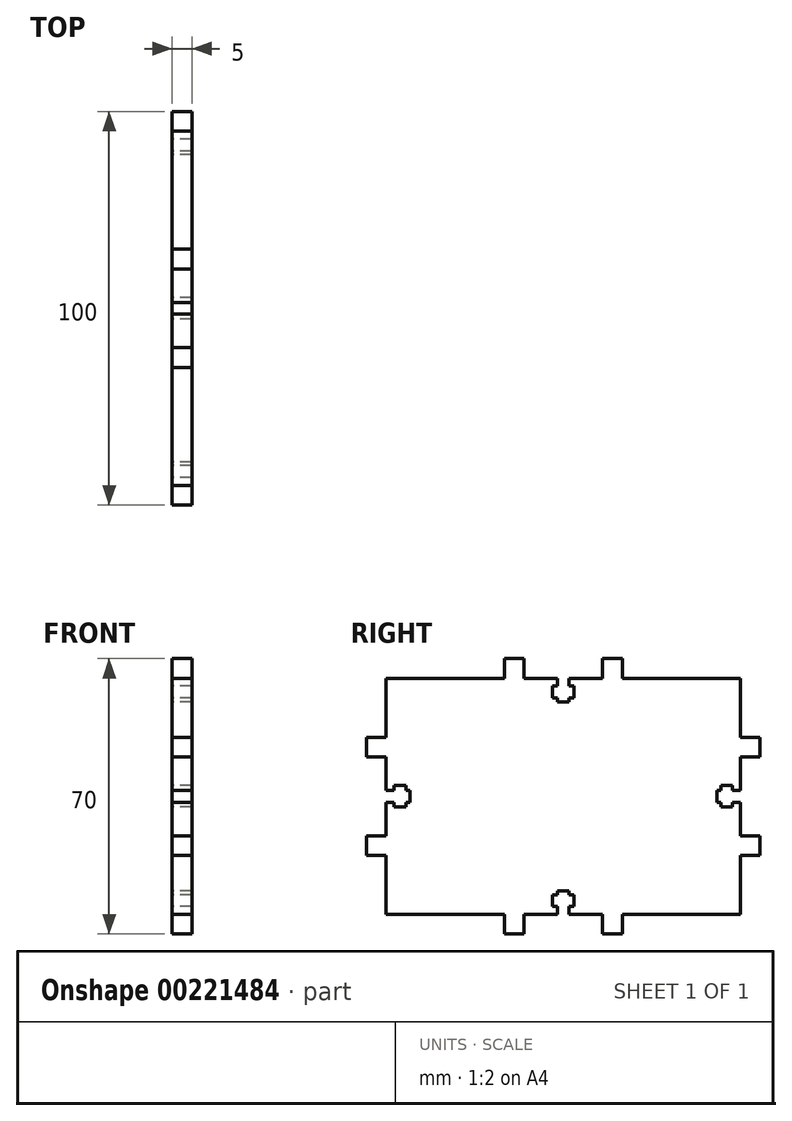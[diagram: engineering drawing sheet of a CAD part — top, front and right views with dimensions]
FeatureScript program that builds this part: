
annotation { "Feature Type Name" : "Feature", "Feature Type Description" : "" }
export const myFeature = defineFeature(function(context is Context, id is Id, definition is map)
    precondition{}
    {
        {
            assignVariable(context, id + "F0", {"name" : "thickness", "anyValue" : 5 * mm});
        }
        {
            var Q0;
            Q0=qCreatedBy(makeId("Right.planeOp"),FACE);
            var sketch = newSketch(context, id + "F1", { "sketchPlane" : qUnion([Q0])});
            skLineSegment(sketch, "E0.bottom", {"start": v(0, 0) * mm, "end": v(30, 0) * mm});
            skLineSegment(sketch, "E0.top", {"start": v(0, 60) * mm, "end": v(30, 60) * mm});
            skLineSegment(sketch, "E0.left", {"start": v(0, 0) * mm, "end": v(0, 15) * mm});
            skLineSegment(sketch, "E0.right", {"start": v(90, 0) * mm, "end": v(90, 15) * mm});
            skLineSegment(sketch, "E1", {"start": v(0, 45) * mm, "end": v(-5, 45) * mm});
            skLineSegment(sketch, "E2", {"start": v(-5, 45) * mm, "end": v(-5, 40) * mm});
            skLineSegment(sketch, "E3", {"start": v(-5, 40) * mm, "end": v(0, 40) * mm});
            skLineSegment(sketch, "E4", {"start": v(0, 20) * mm, "end": v(-5, 20) * mm});
            skLineSegment(sketch, "E5", {"start": v(-5, 20) * mm, "end": v(-5, 15) * mm});
            skLineSegment(sketch, "E6", {"start": v(-5, 15) * mm, "end": v(0, 15) * mm});
            skLineSegment(sketch, "E7", {"start": v(45, 60) * mm, "end": v(45, 0) * mm, "construction": true});
            skLineSegment(sketch, "E8", {"start": v(90, 30) * mm, "end": v(0, 30) * mm, "construction": true});
            skLineSegment(sketch, "E9", {"start": v(0, 31.5) * mm, "end": v(2, 31.5) * mm});
            skLineSegment(sketch, "E10", {"start": v(2, 31.5) * mm, "end": v(2, 32.75) * mm});
            skLineSegment(sketch, "E11", {"start": v(2, 32.75) * mm, "end": v(5, 32.75) * mm});
            skLineSegment(sketch, "E12", {"start": v(5, 32.75) * mm, "end": v(5, 31.5) * mm});
            skLineSegment(sketch, "E13", {"start": v(5, 27.25) * mm, "end": v(2, 27.25) * mm});
            skLineSegment(sketch, "E14", {"start": v(2, 27.25) * mm, "end": v(2, 28.5) * mm});
            skLineSegment(sketch, "E15", {"start": v(2, 28.5) * mm, "end": v(0, 28.5) * mm});
            skLineSegment(sketch, "E16", {"start": v(5, 31.5) * mm, "end": v(6, 31.5) * mm});
            skLineSegment(sketch, "E17", {"start": v(6, 31.5) * mm, "end": v(6, 28.5) * mm});
            skLineSegment(sketch, "E18", {"start": v(6, 28.5) * mm, "end": v(5, 28.5) * mm});
            skLineSegment(sketch, "E19.trimOffspring", {"start": v(5, 28.5) * mm, "end": v(5, 27.25) * mm});
            skPoint(sketch, "E20", {"position": v(6, 30) * mm});
            skLineSegment(sketch, "E21.MirrorCS", {"start": v(85, 31.5) * mm, "end": v(84, 31.5) * mm});
            skLineSegment(sketch, "E22.MirrorCS", {"start": v(88, 31.5) * mm, "end": v(88, 32.75) * mm});
            skLineSegment(sketch, "E23.MirrorCS", {"start": v(84, 28.5) * mm, "end": v(85, 28.5) * mm});
            skLineSegment(sketch, "E24.MirrorCS", {"start": v(88, 27.25) * mm, "end": v(88, 28.5) * mm});
            skLineSegment(sketch, "E25.MirrorCS", {"start": v(85, 32.75) * mm, "end": v(85, 31.5) * mm});
            skLineSegment(sketch, "E26.MirrorCS", {"start": v(85, 28.5) * mm, "end": v(85, 27.25) * mm});
            skLineSegment(sketch, "E27.MirrorCS", {"start": v(88, 28.5) * mm, "end": v(90, 28.5) * mm});
            skLineSegment(sketch, "E28.MirrorCS", {"start": v(84, 31.5) * mm, "end": v(84, 28.5) * mm});
            skLineSegment(sketch, "E29.MirrorCS", {"start": v(90, 31.5) * mm, "end": v(88, 31.5) * mm});
            skPoint(sketch, "E30.MirrorP", {"position": v(84, 30) * mm});
            skLineSegment(sketch, "E31.MirrorCS", {"start": v(85, 27.25) * mm, "end": v(88, 27.25) * mm});
            skLineSegment(sketch, "E32.MirrorCS", {"start": v(90, 45) * mm, "end": v(95, 45) * mm});
            skLineSegment(sketch, "E33.MirrorCS", {"start": v(95, 45) * mm, "end": v(95, 40) * mm});
            skLineSegment(sketch, "E34.MirrorCS", {"start": v(95, 40) * mm, "end": v(90, 40) * mm});
            skLineSegment(sketch, "E35.MirrorCS", {"start": v(88, 32.75) * mm, "end": v(85, 32.75) * mm});
            skLineSegment(sketch, "E36.MirrorCS", {"start": v(95, 15) * mm, "end": v(90, 15) * mm});
            skLineSegment(sketch, "E37.MirrorCS", {"start": v(90, 20) * mm, "end": v(95, 20) * mm});
            skLineSegment(sketch, "E38.MirrorCS", {"start": v(95, 20) * mm, "end": v(95, 15) * mm});
            skLineSegment(sketch, "E39", {"start": v(30, 0) * mm, "end": v(30, -5) * mm});
            skLineSegment(sketch, "E40", {"start": v(30, -5) * mm, "end": v(35, -5) * mm});
            skLineSegment(sketch, "E41", {"start": v(35, -5) * mm, "end": v(35, 0) * mm});
            skLineSegment(sketch, "E42", {"start": v(55, 0) * mm, "end": v(55, -5) * mm});
            skLineSegment(sketch, "E43", {"start": v(55, -5) * mm, "end": v(60, -5) * mm});
            skLineSegment(sketch, "E44", {"start": v(60, -5) * mm, "end": v(60, 0) * mm});
            skLineSegment(sketch, "E45", {"start": v(43.5, 0) * mm, "end": v(43.5, 2) * mm});
            skLineSegment(sketch, "E46", {"start": v(43.5, 2) * mm, "end": v(42.25, 2) * mm});
            skLineSegment(sketch, "E47", {"start": v(42.25, 2) * mm, "end": v(42.25, 5) * mm});
            skLineSegment(sketch, "E48", {"start": v(42.25, 5) * mm, "end": v(43.5, 5) * mm});
            skLineSegment(sketch, "E49", {"start": v(47.75, 5) * mm, "end": v(47.75, 2) * mm});
            skLineSegment(sketch, "E50", {"start": v(47.75, 2) * mm, "end": v(46.5, 2) * mm});
            skLineSegment(sketch, "E51", {"start": v(46.5, 2) * mm, "end": v(46.5, 0) * mm});
            skLineSegment(sketch, "E52", {"start": v(43.5, 5) * mm, "end": v(43.5, 6) * mm});
            skLineSegment(sketch, "E53", {"start": v(43.5, 6) * mm, "end": v(46.5, 6) * mm});
            skLineSegment(sketch, "E54", {"start": v(46.5, 6) * mm, "end": v(46.5, 5) * mm});
            skLineSegment(sketch, "E55.trimOffspring", {"start": v(46.5, 5) * mm, "end": v(47.75, 5) * mm});
            skLineSegment(sketch, "E56.MirrorCS", {"start": v(47.75, 58) * mm, "end": v(46.5, 58) * mm});
            skLineSegment(sketch, "E57.MirrorCS", {"start": v(43.5, 58) * mm, "end": v(42.25, 58) * mm});
            skLineSegment(sketch, "E58.MirrorCS", {"start": v(42.25, 55) * mm, "end": v(43.5, 55) * mm});
            skLineSegment(sketch, "E59.MirrorCS", {"start": v(43.5, 55) * mm, "end": v(43.5, 54) * mm});
            skLineSegment(sketch, "E60.MirrorCS", {"start": v(46.5, 55) * mm, "end": v(47.75, 55) * mm});
            skLineSegment(sketch, "E61.MirrorCS", {"start": v(46.5, 54) * mm, "end": v(46.5, 55) * mm});
            skLineSegment(sketch, "E62.MirrorCS", {"start": v(43.5, 54) * mm, "end": v(46.5, 54) * mm});
            skLineSegment(sketch, "E63.MirrorCS", {"start": v(43.5, 60) * mm, "end": v(43.5, 58) * mm});
            skLineSegment(sketch, "E64.MirrorCS", {"start": v(46.5, 58) * mm, "end": v(46.5, 60) * mm});
            skLineSegment(sketch, "E65.MirrorCS", {"start": v(35, 65) * mm, "end": v(35, 60) * mm});
            skPoint(sketch, "E66.MirrorP", {"position": v(45, 54) * mm});
            skLineSegment(sketch, "E67.MirrorCS", {"start": v(55, 60) * mm, "end": v(55, 65) * mm});
            skLineSegment(sketch, "E68.MirrorCS", {"start": v(47.75, 55) * mm, "end": v(47.75, 58) * mm});
            skLineSegment(sketch, "E69.MirrorCS", {"start": v(30, 65) * mm, "end": v(35, 65) * mm});
            skLineSegment(sketch, "E70.MirrorCS", {"start": v(30, 60) * mm, "end": v(30, 65) * mm});
            skLineSegment(sketch, "E71.MirrorCS", {"start": v(55, 65) * mm, "end": v(60, 65) * mm});
            skLineSegment(sketch, "E72.MirrorCS", {"start": v(42.25, 58) * mm, "end": v(42.25, 55) * mm});
            skLineSegment(sketch, "E73.MirrorCS", {"start": v(60, 65) * mm, "end": v(60, 60) * mm});
            skLineSegment(sketch, "E74.trimOffspring", {"start": v(0, 31.5) * mm, "end": v(0, 40) * mm});
            skLineSegment(sketch, "E75.trimOffspring", {"start": v(0, 45) * mm, "end": v(0, 60) * mm});
            skLineSegment(sketch, "E76.trimOffspring", {"start": v(0, 20) * mm, "end": v(0, 28.5) * mm});
            skLineSegment(sketch, "E77.trimOffspring", {"start": v(35, 0) * mm, "end": v(43.5, 0) * mm});
            skLineSegment(sketch, "E78.trimOffspring", {"start": v(46.5, 0) * mm, "end": v(55, 0) * mm});
            skLineSegment(sketch, "E79.trimOffspring", {"start": v(60, 0) * mm, "end": v(90, 0) * mm});
            skLineSegment(sketch, "E80.trimOffspring", {"start": v(90, 20) * mm, "end": v(90, 28.5) * mm});
            skLineSegment(sketch, "E81.trimOffspring", {"start": v(90, 31.5) * mm, "end": v(90, 40) * mm});
            skLineSegment(sketch, "E82.trimOffspring", {"start": v(90, 45) * mm, "end": v(90, 60) * mm});
            skLineSegment(sketch, "E83.trimOffspring", {"start": v(60, 60) * mm, "end": v(90, 60) * mm});
            skLineSegment(sketch, "E84.trimOffspring", {"start": v(35, 60) * mm, "end": v(43.5, 60) * mm});
            skLineSegment(sketch, "E85.trimOffspring", {"start": v(46.5, 60) * mm, "end": v(55, 60) * mm});
            skSolve(sketch);
        }
        {
            var Q0;
            Q0=makeQuery(id+"F1.imprint","IMPRINT",FACE,{"disambiguationData":[TD([[makeQuery(id+"F1.imprint","IMPRINT",EDGE,{"derivedFrom":sQuery(id+"F1.wireOp",EDGE,"E0.bottom")}),1.0]])]});
            extrude(context, id + "F2", {"entities" : qUnion([Q0]), "depth" : getVariable(context, 'thickness')});
        }
    });
